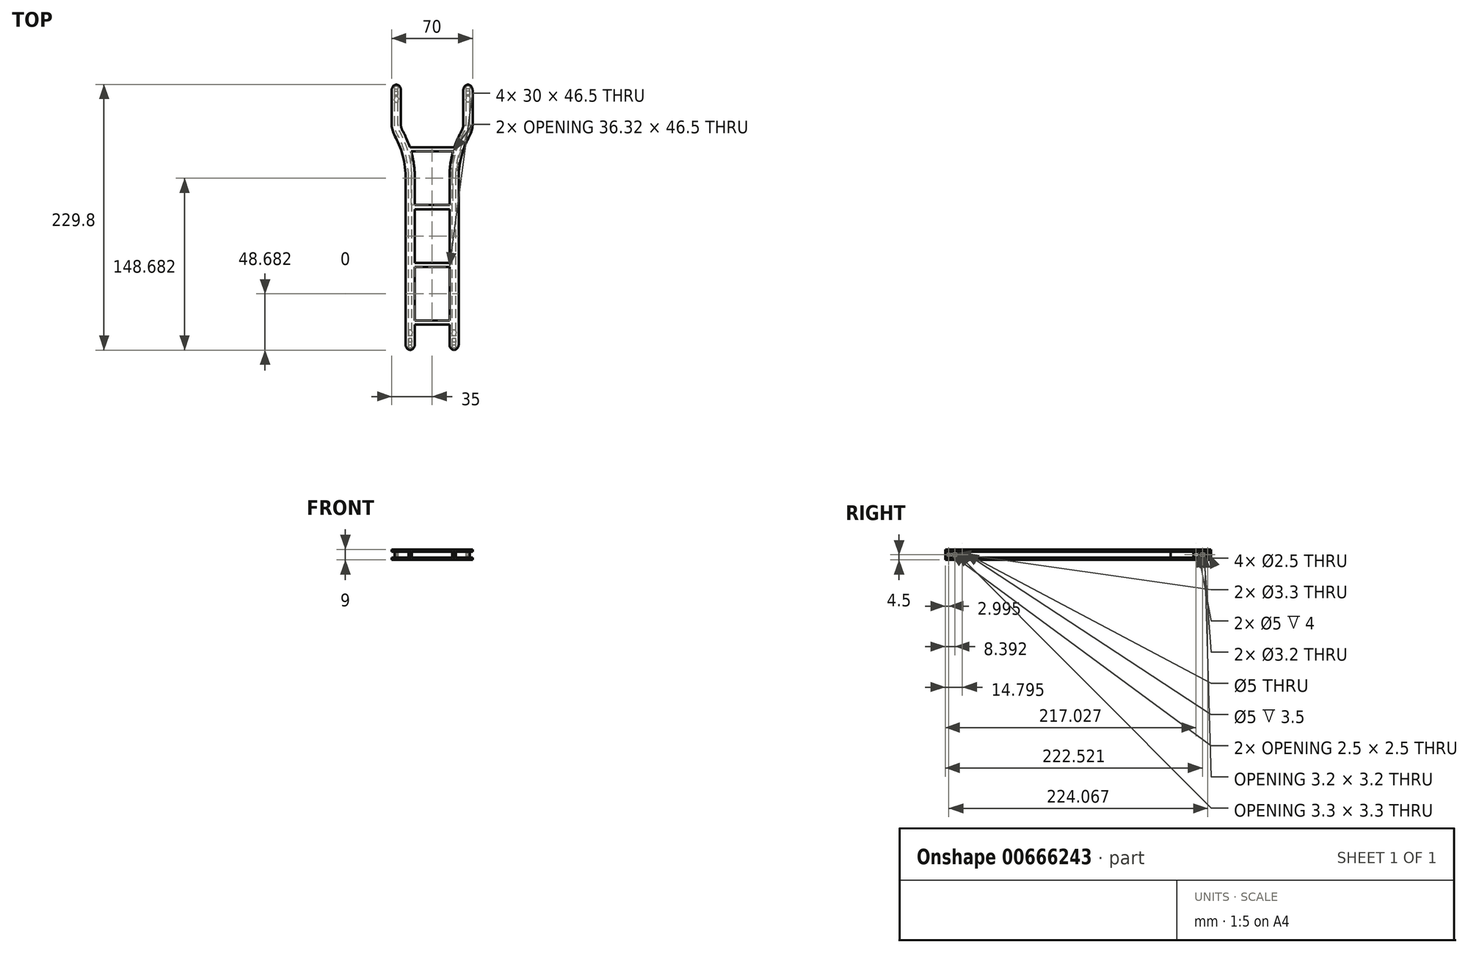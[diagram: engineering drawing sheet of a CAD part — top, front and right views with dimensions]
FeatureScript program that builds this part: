
annotation { "Feature Type Name" : "Feature", "Feature Type Description" : "" }
export const myFeature = defineFeature(function(context is Context, id is Id, definition is map)
    precondition{}
    {
        {
            var Q0;
            Q0=qCreatedBy(makeId("Front.planeOp"),FACE);
            var sketch = newSketch(context, id + "F0", { "sketchPlane" : qUnion([Q0])});
            skLineSegment(sketch, "E0.bottom", {"start": v(-15, 0) * mm, "end": v(-23, 0) * mm});
            skLineSegment(sketch, "E0.top", {"start": v(-15, 9) * mm, "end": v(-23, 9) * mm});
            skLineSegment(sketch, "E0.left", {"start": v(-15, 0) * mm, "end": v(-15, 2) * mm});
            skLineSegment(sketch, "E0.right", {"start": v(-23, 0) * mm, "end": v(-23, 2) * mm});
            skLineSegment(sketch, "E1.bottom", {"start": v(-23, 7) * mm, "end": v(-21, 7) * mm});
            skLineSegment(sketch, "E1.top", {"start": v(-23, 2) * mm, "end": v(-21, 2) * mm});
            skLineSegment(sketch, "E1.right", {"start": v(-20.5, 6.5) * mm, "end": v(-20.5, 2.5) * mm});
            skLineSegment(sketch, "E2.bottom", {"start": v(-17, 7) * mm, "end": v(-15, 7) * mm});
            skLineSegment(sketch, "E2.top", {"start": v(-17, 2) * mm, "end": v(-15, 2) * mm});
            skLineSegment(sketch, "E2.left", {"start": v(-17.5, 6.5) * mm, "end": v(-17.5, 2.5) * mm});
            skLineSegment(sketch, "E3", {"start": v(-19, 9) * mm, "end": v(-19, -4.59) * mm, "construction": true});
            skPoint(sketch, "E3.endSnap0", {"position": v(-19, 0) * mm});
            skLineSegment(sketch, "E4.trimOffspring", {"start": v(-15, 7) * mm, "end": v(-15, 9) * mm});
            skLineSegment(sketch, "E5.trimOffspring", {"start": v(-23, 7) * mm, "end": v(-23, 9) * mm});
            skPoint(sketch, "E6.visualSharp", {"position": v(-20.5, 7) * mm});
            skArc(sketch, "E6.filletArc", {"start": v(-20.5, 6.5) * mm, "mid": v(-20.65, 6.85) * mm, "end": v(-21, 7) * mm});
            skPoint(sketch, "E7.visualSharp", {"position": v(-17.5, 7) * mm});
            skArc(sketch, "E7.filletArc", {"start": v(-17, 7) * mm, "mid": v(-17.35, 6.85) * mm, "end": v(-17.5, 6.5) * mm});
            skPoint(sketch, "E8.visualSharp", {"position": v(-17.5, 2) * mm});
            skArc(sketch, "E8.filletArc", {"start": v(-17.5, 2.5) * mm, "mid": v(-17.35, 2.15) * mm, "end": v(-17, 2) * mm});
            skPoint(sketch, "E9.visualSharp", {"position": v(-20.5, 2) * mm});
            skArc(sketch, "E9.filletArc", {"start": v(-21, 2) * mm, "mid": v(-20.65, 2.15) * mm, "end": v(-20.5, 2.5) * mm});
            skSolve(sketch);
        }
        {
            var Q0;
            Q0=qCreatedBy(makeId("Top.planeOp"),FACE);
            var sketch = newSketch(context, id + "F1", { "sketchPlane" : qUnion([Q0])});
            skLineSegment(sketch, "E10", {"start": v(-35.26, 0) * mm, "end": v(-35.26, 150) * mm});
            skLineSegment(sketch, "E11", {"start": v(-47.26, 230) * mm, "end": v(-47.26, 195) * mm});
            skFitSpline(sketch, "E12", {"points": [v(-35.26, 150) * mm, v(-40.7, 174.86) * mm, v(-47.26, 195) * mm], "startDerivative": vector(-0.38, 53.31) * mm, "endDerivative": vector(-0.87, 58.08) * mm});
            skSolve(sketch);
        }
        {
            var Q0;
            Q0=qSketchRegion(id+"F0",true);
            var Q1;
            Q1=qConstructionFilter(qBodyType(qCreatedBy(id+"F1",EDGE),BodyType.WIRE),ConstructionObject.NO);
            sweep(context, id + "F2", {"profiles" : qUnion([Q0]), "path" : qUnion([Q1])});
        }
        {
            var Q0;
            Q0=makeQuery(id+"F2.opSweep","SWEPT_FACE",FACE,{"disambiguationData":[OSD([sQuery(id+"F0.wireOp",EDGE,"E4.trimOffspring"),sQuery(id+"F1.wireOp",EDGE,"E10")])]});
            var sketch = newSketch(context, id + "F3", { "sketchPlane" : qUnion([Q0])});
            skLineSegment(sketch, "E13.bottom", {"start": v(22.03, 9) * mm, "end": v(25.53, 9) * mm});
            skLineSegment(sketch, "E13.top", {"start": v(22.03, 7) * mm, "end": v(25.53, 7) * mm});
            skLineSegment(sketch, "E13.left", {"start": v(22.03, 9) * mm, "end": v(22.03, 7) * mm});
            skLineSegment(sketch, "E13.right", {"start": v(25.53, 9) * mm, "end": v(25.53, 7) * mm});
            skLineSegment(sketch, "E14.0.1.0", {"start": v(22.03, 2) * mm, "end": v(22.03, 0) * mm});
            skLineSegment(sketch, "E14.0.1.1", {"start": v(22.03, 0) * mm, "end": v(25.53, 0) * mm});
            skLineSegment(sketch, "E14.0.1.2", {"start": v(22.03, 2) * mm, "end": v(25.53, 2) * mm});
            skLineSegment(sketch, "E14.0.1.3", {"start": v(25.53, 2) * mm, "end": v(25.53, 0) * mm});
            skLineSegment(sketch, "E14.1.0.0", {"start": v(72.03, 9) * mm, "end": v(72.03, 7) * mm});
            skLineSegment(sketch, "E14.1.0.1", {"start": v(72.03, 7) * mm, "end": v(75.53, 7) * mm});
            skLineSegment(sketch, "E14.1.0.2", {"start": v(72.03, 9) * mm, "end": v(75.53, 9) * mm});
            skLineSegment(sketch, "E14.1.0.3", {"start": v(75.53, 9) * mm, "end": v(75.53, 7) * mm});
            skLineSegment(sketch, "E14.1.1.0", {"start": v(72.03, 2) * mm, "end": v(72.03, 0) * mm});
            skLineSegment(sketch, "E14.1.1.1", {"start": v(72.03, 0) * mm, "end": v(75.53, 0) * mm});
            skLineSegment(sketch, "E14.1.1.2", {"start": v(72.03, 2) * mm, "end": v(75.53, 2) * mm});
            skLineSegment(sketch, "E14.1.1.3", {"start": v(75.53, 2) * mm, "end": v(75.53, 0) * mm});
            skLineSegment(sketch, "E14.2.0.0", {"start": v(122.03, 9) * mm, "end": v(122.03, 7) * mm});
            skLineSegment(sketch, "E14.2.0.1", {"start": v(122.03, 7) * mm, "end": v(125.53, 7) * mm});
            skLineSegment(sketch, "E14.2.0.2", {"start": v(122.03, 9) * mm, "end": v(125.53, 9) * mm});
            skLineSegment(sketch, "E14.2.0.3", {"start": v(125.53, 9) * mm, "end": v(125.53, 7) * mm});
            skLineSegment(sketch, "E14.2.1.0", {"start": v(122.03, 2) * mm, "end": v(122.03, 0) * mm});
            skLineSegment(sketch, "E14.2.1.1", {"start": v(122.03, 0) * mm, "end": v(125.53, 0) * mm});
            skLineSegment(sketch, "E14.2.1.2", {"start": v(122.03, 2) * mm, "end": v(125.53, 2) * mm});
            skLineSegment(sketch, "E14.2.1.3", {"start": v(125.53, 2) * mm, "end": v(125.53, 0) * mm});
            skLineSegment(sketch, "E14.3.0.0", {"start": v(172.03, 9) * mm, "end": v(172.03, 7) * mm});
            skLineSegment(sketch, "E14.3.0.1", {"start": v(172.03, 7) * mm, "end": v(175.53, 7) * mm});
            skLineSegment(sketch, "E14.3.0.2", {"start": v(172.03, 9) * mm, "end": v(175.53, 9) * mm});
            skLineSegment(sketch, "E14.3.0.3", {"start": v(175.53, 9) * mm, "end": v(175.53, 7) * mm});
            skLineSegment(sketch, "E14.3.1.0", {"start": v(172.03, 2) * mm, "end": v(172.03, 0) * mm});
            skLineSegment(sketch, "E14.3.1.1", {"start": v(172.03, 0) * mm, "end": v(175.53, 0) * mm});
            skLineSegment(sketch, "E14.3.1.2", {"start": v(172.03, 2) * mm, "end": v(175.53, 2) * mm});
            skLineSegment(sketch, "E14.3.1.3", {"start": v(175.53, 2) * mm, "end": v(175.53, 0) * mm});
            skLineSegment(sketch, "E14.direction1", {"start": v(22.03, 7) * mm, "end": v(72.03, 7) * mm, "construction": true});
            skLineSegment(sketch, "E14.direction2", {"start": v(22.03, 7) * mm, "end": v(22.03, 0) * mm, "construction": true});
            skSolve(sketch);
        }
        {
            var Q0;
            Q0=qSketchRegion(id+"F3",true);
            extrude(context, id + "F4", {"entities" : qUnion([Q0]), "operationType" : NewBodyOperationType.ADD, "depth" : 15 * mm});
        }
        {
            var Q0;
            Q0=makeQuery(id+"F4.opExtrude","CAP_FACE",FACE,{"disambiguationData":[OSD([sQuery(id+"F3.wireOp",EDGE,"E14.3.0.0"),sQuery(id+"F3.wireOp",EDGE,"E14.3.0.1"),sQuery(id+"F3.wireOp",EDGE,"E14.3.0.2"),sQuery(id+"F3.wireOp",EDGE,"E14.3.0.3")])],"isStart":true});
            var sketch = newSketch(context, id + "F5", { "sketchPlane" : qUnion([Q0])});
            skLineSegment(sketch, "E15.0", {"start": v(-172.03, 7) * mm, "end": v(-175.53, 7) * mm});
            skLineSegment(sketch, "E16.0.0", {"start": v(-175.53, 9) * mm, "end": v(-175.53, 7) * mm});
            skLineSegment(sketch, "E16.0.1", {"start": v(-175.53, 7) * mm, "end": v(-172.03, 7) * mm});
            skLineSegment(sketch, "E16.0.2", {"start": v(-172.03, 7) * mm, "end": v(-172.03, 9) * mm});
            skLineSegment(sketch, "E16.0.3", {"start": v(-172.03, 9) * mm, "end": v(-175.53, 9) * mm});
            skLineSegment(sketch, "E17.0.0", {"start": v(-175.53, 2) * mm, "end": v(-175.53, 0) * mm});
            skLineSegment(sketch, "E17.0.1", {"start": v(-175.53, 0) * mm, "end": v(-172.03, 0) * mm});
            skLineSegment(sketch, "E17.0.2", {"start": v(-172.03, 0) * mm, "end": v(-172.03, 2) * mm});
            skLineSegment(sketch, "E17.0.3", {"start": v(-172.03, 2) * mm, "end": v(-175.53, 2) * mm});
            skSolve(sketch);
        }
        {
            var Q0;
            Q0=qSketchRegion(id+"F5",true);
            extrude(context, id + "F6", {"entities" : qUnion([Q0]), "operationType" : NewBodyOperationType.ADD, "endBound" : BoundingType.UP_TO_NEXT, "depth" : 25 * mm});
        }
        {
            var Q0;
            Q0=makeQuery(id+"F2.opSweep","SWEPT_BODY",BODY,{"disambiguationData":[OSD([sQuery(id+"F0.wireOp",EDGE,"E0.bottom"),sQuery(id+"F0.wireOp",EDGE,"E0.top"),sQuery(id+"F0.wireOp",EDGE,"E0.left"),sQuery(id+"F0.wireOp",EDGE,"E0.right"),sQuery(id+"F0.wireOp",EDGE,"E1.bottom"),sQuery(id+"F0.wireOp",EDGE,"E1.top"),sQuery(id+"F0.wireOp",EDGE,"E1.right"),sQuery(id+"F0.wireOp",EDGE,"E2.bottom"),sQuery(id+"F0.wireOp",EDGE,"E2.top"),sQuery(id+"F0.wireOp",EDGE,"E2.left"),sQuery(id+"F0.wireOp",EDGE,"E4.trimOffspring"),sQuery(id+"F0.wireOp",EDGE,"E5.trimOffspring"),sQuery(id+"F0.wireOp",EDGE,"E6.filletArc"),sQuery(id+"F0.wireOp",EDGE,"E7.filletArc"),sQuery(id+"F0.wireOp",EDGE,"E8.filletArc"),sQuery(id+"F0.wireOp",EDGE,"E9.filletArc"),sQuery(id+"F1.wireOp",EDGE,"E11")])]});
            var Q1;
            Q1=makeQuery(id+"F4.opExtrude","CAP_FACE",FACE,{"disambiguationData":[OSD([sQuery(id+"F3.wireOp",EDGE,"E14.1.0.0"),sQuery(id+"F3.wireOp",EDGE,"E14.1.0.1"),sQuery(id+"F3.wireOp",EDGE,"E14.1.0.2"),sQuery(id+"F3.wireOp",EDGE,"E14.1.0.3")])],"isStart":false});
            mirror(context, id + "F7", {"operationType" : NewBodyOperationType.ADD, "entities" : qUnion([Q0]), "mirrorPlane" : qUnion([Q1])});
        }
        {
            var Q0;
            Q0=makeQuery(id+"F2.opSweep","SWEPT_FACE",FACE,{"disambiguationData":[OSD([sQuery(id+"F0.wireOp",EDGE,"E1.right"),sQuery(id+"F1.wireOp",EDGE,"E10")])]});
            var sketch = newSketch(context, id + "F8", { "sketchPlane" : qUnion([Q0])});
            skCircle(sketch, "E18", {"center": v(-14.9, 4.5) * mm, "radius": 2.5 * mm});
            skPoint(sketch, "E18.centerSnap0", {"position": v(0, 4.5) * mm});
            skCircle(sketch, "E19", {"center": v(-3.1, 4.5) * mm, "radius": 1.25 * mm});
            skCircle(sketch, "E20", {"center": v(-8.5, 4.5) * mm, "radius": 1.65 * mm});
            skLineSegment(sketch, "E21", {"start": v(-230, 4.5) * mm, "end": v(-219.48, 4.5) * mm, "construction": true});
            skCircle(sketch, "E22", {"center": v(-227.16, 4.5) * mm, "radius": 1.25 * mm});
            skCircle(sketch, "E23", {"center": v(-222.62, 4.5) * mm, "radius": 1.6 * mm});
            skCircle(sketch, "E24", {"center": v(-217.13, 4.5) * mm, "radius": 2.5 * mm});
            skSolve(sketch);
        }
        {
            var Q0;
            Q0=qSketchRegion(id+"F8",true);
            extrude(context, id + "F9", {"entities" : qUnion([Q0]), "operationType" : NewBodyOperationType.REMOVE, "endBound" : BoundingType.THROUGH_ALL, "oppositeDirection" : true, "depth" : 25 * mm});
        }
        {
            var Q0;
            {var subQ0=sQuery(id+"F1.wireOp",EDGE,"E11");var subQ3=sQuery(id+"F1.wireOp",EDGE,"E12");var subQ4=sQuery(id+"F0.wireOp",EDGE,"E1.right");Q0=makeQuery(id+"F9.boolean.opBoolean","SPLIT",FACE,{"disambiguationData":[TD([makeQuery(id+"F7.opPattern","COPY",FACE,{"derivedFrom":makeQuery(id+"F2.opSweep","SWEPT_FACE",FACE,{"disambiguationData":[OSD([subQ4,subQ3])]}),"instanceName":"1"})])],"derivedFrom":makeQuery(id+"F7.opPattern","COPY",FACE,{"derivedFrom":makeQuery(id+"F2.opSweep","SWEPT_FACE",FACE,{"disambiguationData":[OSD([subQ4,subQ0])]}),"instanceName":"1"})});}
            var sketch = newSketch(context, id + "F10", { "sketchPlane" : qUnion([Q0])});
            skArc(sketch, "E25.0", {"start": v(218.63, 2.5) * mm, "mid": v(219.63, 4.5) * mm, "end": v(218.63, 6.5) * mm});
            skArc(sketch, "E26.0", {"start": v(215.63, 6.5) * mm, "mid": v(214.63, 4.5) * mm, "end": v(215.63, 2.5) * mm});
            skArc(sketch, "E27.0", {"start": v(215.63, 6.5) * mm, "mid": v(216.34, 6.87) * mm, "end": v(217.13, 7) * mm});
            skArc(sketch, "E28.0", {"start": v(217.13, 7) * mm, "mid": v(217.92, 6.87) * mm, "end": v(218.63, 6.5) * mm});
            skArc(sketch, "E29.0", {"start": v(217.13, 2) * mm, "mid": v(216.34, 2.13) * mm, "end": v(215.63, 2.5) * mm});
            skArc(sketch, "E30.0", {"start": v(218.63, 2.5) * mm, "mid": v(217.92, 2.13) * mm, "end": v(217.13, 2) * mm});
            skCircle(sketch, "E31.0", {"center": v(222.62, 4.5) * mm, "radius": 1.6 * mm});
            skCircle(sketch, "E32.0", {"center": v(227.16, 4.5) * mm, "radius": 1.25 * mm});
            skSolve(sketch);
        }
        {
            var Q0;
            Q0=qSketchRegion(id+"F10",true);
            extrude(context, id + "F11", {"entities" : qUnion([Q0]), "operationType" : NewBodyOperationType.REMOVE, "endBound" : BoundingType.THROUGH_ALL, "oppositeDirection" : true, "depth" : 25 * mm});
        }
        {
            var Q0;
            Q0=makeQuery(id+"F7.opPattern","COPY",EDGE,{"derivedFrom":makeQuery(id+"F2.opSweep","CAP_EDGE",EDGE,{"disambiguationData":[OSD([sQuery(id+"F0.wireOp",EDGE,"E5.trimOffspring"),sQuery(id+"F1.wireOp",VERTEX,"E11.start")])],"isStart":false}),"instanceName":"1"});
            var Q1;
            Q1=makeQuery(id+"F7.opPattern","COPY",EDGE,{"derivedFrom":makeQuery(id+"F2.opSweep","CAP_EDGE",EDGE,{"disambiguationData":[OSD([sQuery(id+"F0.wireOp",EDGE,"E4.trimOffspring"),sQuery(id+"F1.wireOp",VERTEX,"E11.start")])],"isStart":false}),"instanceName":"1"});
            var Q2;
            Q2=makeQuery(id+"F2.opSweep","CAP_EDGE",EDGE,{"disambiguationData":[OSD([sQuery(id+"F0.wireOp",EDGE,"E4.trimOffspring"),sQuery(id+"F1.wireOp",VERTEX,"E11.start")])],"isStart":false});
            var Q3;
            Q3=makeQuery(id+"F2.opSweep","CAP_EDGE",EDGE,{"disambiguationData":[OSD([sQuery(id+"F0.wireOp",EDGE,"E5.trimOffspring"),sQuery(id+"F1.wireOp",VERTEX,"E11.start")])],"isStart":false});
            var Q4;
            Q4=makeQuery(id+"F2.opSweep","CAP_EDGE",EDGE,{"disambiguationData":[OSD([sQuery(id+"F0.wireOp",EDGE,"E4.trimOffspring"),sQuery(id+"F1.wireOp",VERTEX,"E10.start")])],"isStart":true});
            var Q5;
            Q5=makeQuery(id+"F2.opSweep","CAP_EDGE",EDGE,{"disambiguationData":[OSD([sQuery(id+"F0.wireOp",EDGE,"E5.trimOffspring"),sQuery(id+"F1.wireOp",VERTEX,"E10.start")])],"isStart":true});
            var Q6;
            Q6=makeQuery(id+"F7.opPattern","COPY",EDGE,{"derivedFrom":makeQuery(id+"F2.opSweep","CAP_EDGE",EDGE,{"disambiguationData":[OSD([sQuery(id+"F0.wireOp",EDGE,"E5.trimOffspring"),sQuery(id+"F1.wireOp",VERTEX,"E10.start")])],"isStart":true}),"instanceName":"1"});
            var Q7;
            Q7=makeQuery(id+"F7.opPattern","COPY",EDGE,{"derivedFrom":makeQuery(id+"F2.opSweep","CAP_EDGE",EDGE,{"disambiguationData":[OSD([sQuery(id+"F0.wireOp",EDGE,"E4.trimOffspring"),sQuery(id+"F1.wireOp",VERTEX,"E10.start")])],"isStart":true}),"instanceName":"1"});
            fillet(context, id + "F12", {"entities" : qUnion([Q0, Q1, Q2, Q3, Q4, Q5, Q6, Q7]), "radius" : 5 * mm, "tangentPropagation" : true, "allowEdgeOverflow" : false});
        }
    });
